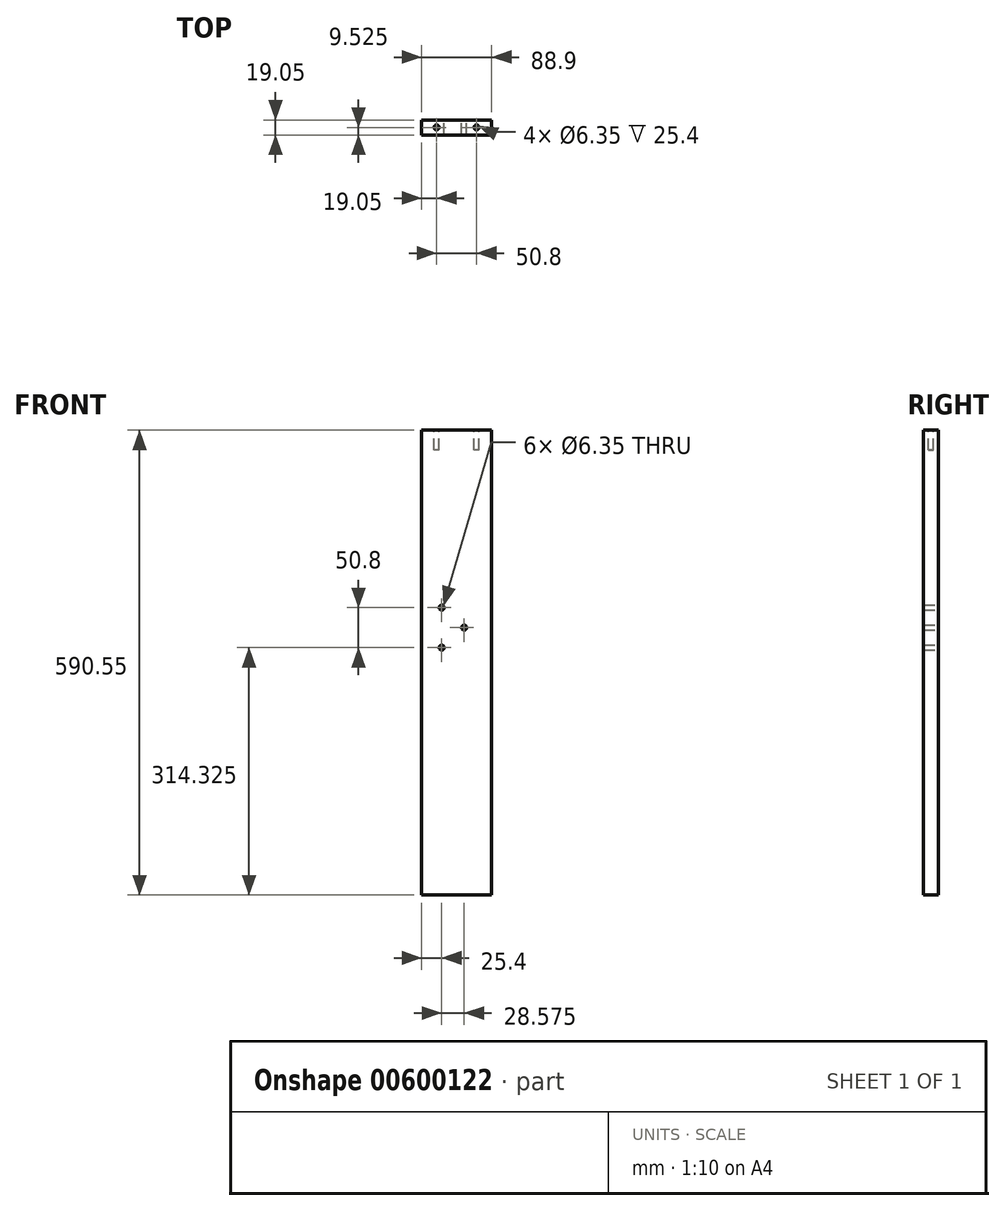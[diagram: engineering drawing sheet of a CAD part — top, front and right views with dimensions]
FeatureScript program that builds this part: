
annotation { "Feature Type Name" : "Feature", "Feature Type Description" : "" }
export const myFeature = defineFeature(function(context is Context, id is Id, definition is map)
    precondition{}
    {
        {
            var Q0;
            Q0=qCreatedBy(makeId("Front.planeOp"),FACE);
            var sketch = newSketch(context, id + "F0", { "sketchPlane" : qUnion([Q0])});
            skLineSegment(sketch, "E0.bottom", {"start": v(0, 0) * mm, "end": v(-88.9, 0) * mm});
            skLineSegment(sketch, "E0.top", {"start": v(0, 590.55) * mm, "end": v(-88.9, 590.55) * mm});
            skLineSegment(sketch, "E0.left", {"start": v(0, 0) * mm, "end": v(0, 590.55) * mm});
            skLineSegment(sketch, "E0.right", {"start": v(-88.9, 0) * mm, "end": v(-88.9, 590.55) * mm});
            skLineSegment(sketch, "E1", {"start": v(-63.5, 365.12) * mm, "end": v(-63.5, 314.33) * mm, "construction": true});
            skLineSegment(sketch, "E2", {"start": v(-63.5, 314.32) * mm, "end": v(-34.93, 339.72) * mm, "construction": true});
            skLineSegment(sketch, "E3", {"start": v(-34.93, 339.73) * mm, "end": v(-63.5, 365.12) * mm, "construction": true});
            skCircle(sketch, "E4", {"center": v(-63.5, 365.12) * mm, "radius": 3.18 * mm});
            skCircle(sketch, "E5", {"center": v(-34.93, 339.73) * mm, "radius": 3.18 * mm});
            skCircle(sketch, "E6", {"center": v(-63.5, 314.33) * mm, "radius": 3.18 * mm});
            skSolve(sketch);
        }
        {
            var Q0;
            Q0 = qSketchRegion(id + "F0", true);
            extrude(context, id + "F1", {"entities" : qUnion([Q0]), "depth" : 19.05 * mm, "offsetDistance" : 25.4 * mm});
        }
        {
            var Q0;
            Q0=makeQuery(id+"F1.opExtrude","SWEPT_FACE",FACE,{"disambiguationData":[OSD([sQuery(id+"F0.wireOp",EDGE,"E0.top")])]});
            var sketch = newSketch(context, id + "F2", { "sketchPlane" : qUnion([Q0])});
            skLineSegment(sketch, "E7.0.0", {"start": v(0, 0) * mm, "end": v(-88.9, 0) * mm, "construction": true});
            skLineSegment(sketch, "E7.0.1", {"start": v(-88.9, 0) * mm, "end": v(-88.9, -19.05) * mm, "construction": true});
            skLineSegment(sketch, "E7.0.2", {"start": v(-88.9, -19.05) * mm, "end": v(0, -19.05) * mm, "construction": true});
            skLineSegment(sketch, "E7.0.3", {"start": v(0, -19.05) * mm, "end": v(0, 0) * mm, "construction": true});
            skLineSegment(sketch, "E8", {"start": v(-88.9, -9.53) * mm, "end": v(-69.85, -9.53) * mm, "construction": true});
            skLineSegment(sketch, "E9", {"start": v(-69.85, -9.53) * mm, "end": v(-19.05, -9.53) * mm, "construction": true});
            skLineSegment(sketch, "E10", {"start": v(-19.05, -9.52) * mm, "end": v(0, -9.52) * mm, "construction": true});
            skCircle(sketch, "E11", {"center": v(-69.85, -9.53) * mm, "radius": 3.18 * mm});
            skCircle(sketch, "E12", {"center": v(-19.05, -9.52) * mm, "radius": 3.18 * mm});
            skSolve(sketch);
        }
        {
            var Q0;
            Q0 = qSketchRegion(id + "F2", true);
            extrude(context, id + "F3", {"entities" : qUnion([Q0]), "operationType" : NewBodyOperationType.REMOVE, "oppositeDirection" : true, "depth" : 25.4 * mm, "offsetDistance" : 25.4 * mm});
        }
    });
